# Revit family: Gira_514500
name_source: partatom
category: Allgemeines Modell
revit_build: Autodesk Revit 2017 (Build: 20160225_1515(x64)
units: mm (PartAtom-declared; Revit-internal decimal feet)

## family parameters
Basisbauteil = Fläche
Beim Laden mit Abzugskörper schneiden = Nein
Bemaßung runder Anschluss = Durchmesser verwenden
Gemeinsam genutzt = Nein
Kann Basisbauteil für Bewehrung sein = Nein
Raumberechnungspunkt = Nein
Teiletyp = Normal

## types (1)
- Gira_514500
    Andere Bussysteme = ohne
    Anzahl der Betätigungspunkte = 12
    Anzahl der Tasten = 6
    Ausführung der Oberfläche = nicht zutreffend
    BIM = https://media.stage.bim.site
    Beschreibung = KNX Tastsensor 3 Plus 5fach (2+3) System 55, Gira E22 Inbetriebnahme-Wippe Merkmale: - Montage auf Busankoppler 3 oder Busankoppler 3 externer Fühler. - Demontageschutz durch Verschraubung. - Grafikdisplay mit Hintergrundbeleuchtung und vielfältigen Anzeigemöglichkeiten, z. B. Temperatur, Uhrzeit, Datum, Alarm- und Hinweistexte. - Zwei mehrfarbige Status-LEDs je Bedienfläche. - Mehrfarbige Status-LED (rot, grün, blau) über die ETS parametrierbar. - Beschriftungsfeldbeleuchtung bei Wippensets mit Beschriftungsfeld. - Interner Temperatursensor zum Messen der lokalen Raumtemperatur. Tastsensor-Eigenschaften:: - Wippen- oder Tastenfunktion für jede Bedienfläche einstellbar. - Wippenfunktion: Schalten, Dimmen, Jalousiesteuerung, Wertgeber 1 Byte, Wertgeber 2 Byte, Szenennebenstelle, 2-Kanal-Bedienung und manuelle Lüftersteuerung. - Tastenfunktion: Schalten, Dimmen, Jalousiesteuerung, Wertgeber 1 Byte, Wertgeber 2 Byte, Szenennebenstelle, 2-Kanal-Bedienung, Reglernebenstelle, Reglerbedienung, Heizungsuhrbedienung und manuelle Lüftersteuerung. - Reglernebenstelle oder Reglerbedienung: Betriebsmodusumschaltung, (definierte Wahl eines Betriebsmodus oder Wechsel zwischen verschiedenen Betriebsmodi bei Reglernebenstelle), Wechsel des Präsenzzustands, Sollwertverschiebung. - Sperrobjekt zum Sperren von einzelnen Tasten- bzw. Wippenfunktionen. - Anzeige einer Alarmmeldung durch Blinken sämtlicher LEDs. - Mehrfarbige Status-LED (rot, grün, blau) ist global oder jeweils getrennt konfigurierbar. Über den Bus kann eine überlagerte Funktion aktiviert werden, wodurch Farbe und Anzeigeinformation einzelner Status-LEDs prioritätsbedingt verändert werden können. - Beschriftungsfeldbeleuchtung EIN, AUS, automatische Abschaltung oder über Objekt schaltbar. - Kommunikationsobjekt zur Helligkeitssteuerung der Status-LED, Beschriftungsfeldbeleuchtung und Hintergrundbeleuchtung des Displays. Raumtemperaturregler-Eigenschaften:: - Betriebsmodi: Komfort, Stand-by, Nacht und Frost- bzw. Hitzeschutz mit jeweils eigenen Temperatursollwerten (für Heizen und bzw. oder Kühlen). - Komfortverlängerung durch Präsenztaste. - Frost- bzw. Hitzeschutzumschaltung durch Fensterstatus oder durch Frostschutzautomatik. - Anzeige der Raumtemperaturregler-Informationen über das Gerätedisplay. - Wahlweise ein oder zwei Regelkreise. - Je Heiz- oder Kühlstufe sind verschiedene Regelungsarten konfigurierbar: PI-Regelung (stetige oder schaltende PWM) oder 2-Punkt-Regelung (schaltend). - Regelparameter für PI-Regler und 2-Punkt-Regler einstellbar. - Interner Temperatursensor und bis zu zwei externe Temperaturfühler (1 x Objekt, 1 x bedrahtet) zur Raumtemperaturmessung möglich. - Optionaler externer bedrahteter Fernfühler bei Fußbodenheizung. - Heizungsuhr mit 28 Schaltzeiten. LC-Display Eigenschaften:: - Grafikdisplay mit schaltbarer LED-Hintergrundbeleuchtung. - 1-Bereichs- oder 2-Bereichsdarstellung. - Textanzeigen im Display in den Sprachen: Deutsch, Englisch, Niederländisch, Norwegisch, Russisch und Polnisch. Weitere Sprachen im Internet verfügbar.  Hinweise : - Professionelle Beschriftung über den Gira Beschriftungsservice www.beschriftung.gira.de. - Der Tastsensor wird mit einer programmneutralen Inbetriebnahme-Wippe geliefert. Das passende Wippenset zum Schalterprogramm ist separat zu bestellen.
    Bussystem Funkbus = Nein
    Bussystem KNX = Ja
    Bussystem KNX-Funk = Nein
    Bussystem LON = Nein
    Bussystem Powernet = Nein
    Datenblatt = https://katalog.gira.de
    Farbe = sonstige
    GTIN = 4010337086895
    HAN = 514500
    Hersteller = Gira
    Mit Beschriftungsfeld = Nein
    Mit Busankopplung = Nein
    Mit Diebstahl-/Demontageschutz = Ja
    Mit Display = Ja
    Mit Infrarotsensor = Nein
    Mit LED-Anzeige = Ja
    Mit Raumthermostat = Ja
    Montageart = Unterputz
    Oberfläche = sonstige
    Produktseite = http://katalog.gira.de
    Schutzart (IP) = IP20
    Transparent = Nein
    Typname = KNX Tastsens.3 Plus 5f (2+3) System 55, Gira E22
    URL = https://www.gira.de
    Vorgabe-Ansicht = 1219 mm
    Werkstoff = sonstige
    Werkstoffgüte = sonstige

## geometry (parser evidence)
native form markers: Sweep x2
no freeform markers — native parametric forms only
